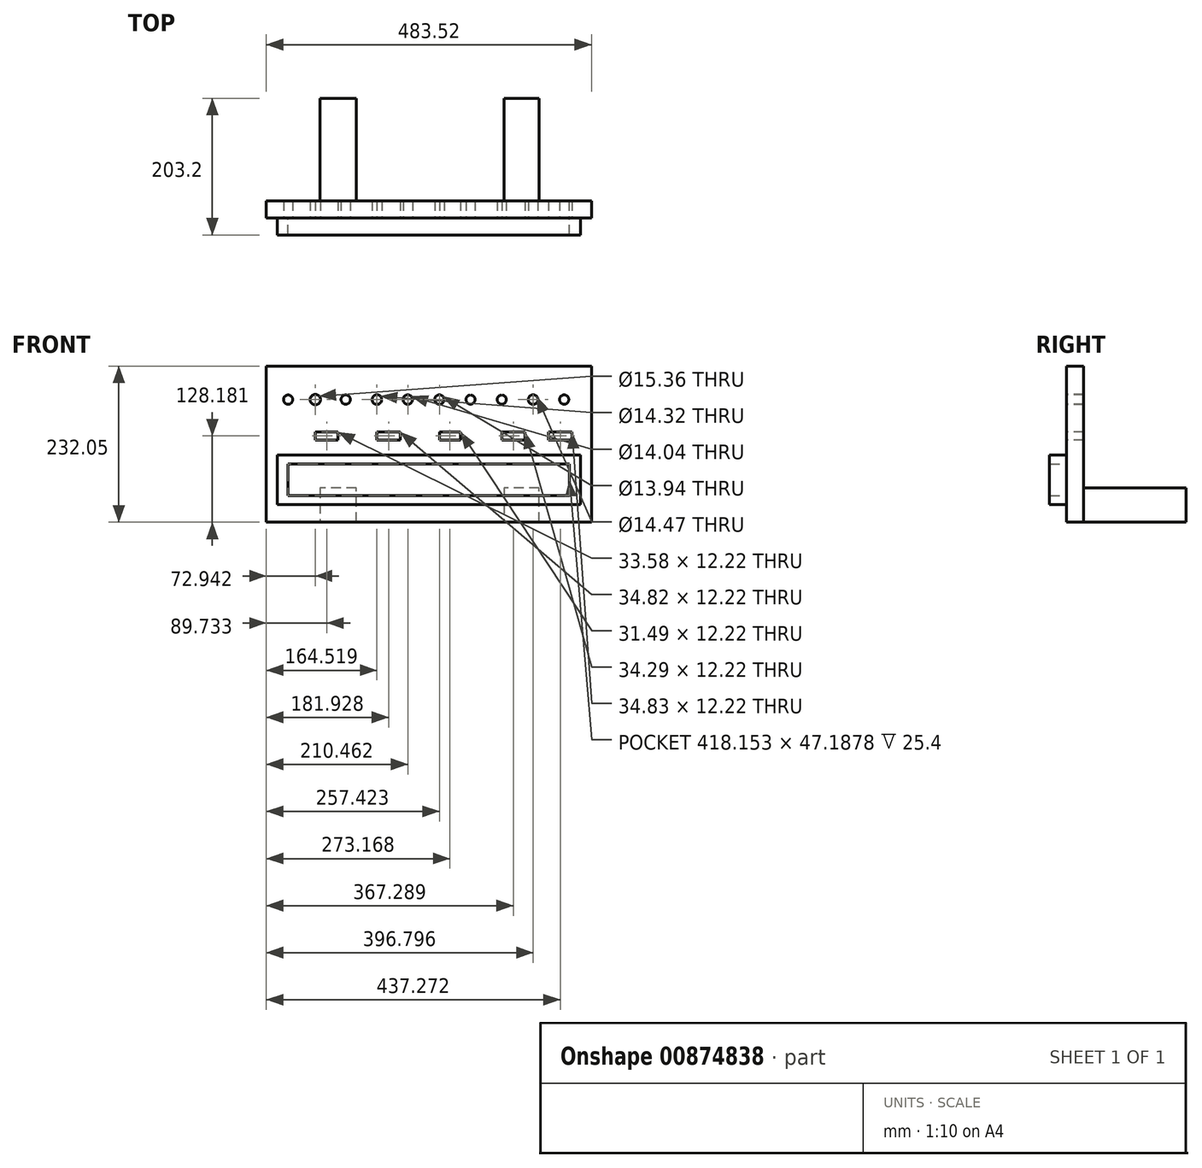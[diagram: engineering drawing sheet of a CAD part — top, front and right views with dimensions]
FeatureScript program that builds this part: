
annotation { "Feature Type Name" : "Feature", "Feature Type Description" : "" }
export const myFeature = defineFeature(function(context is Context, id is Id, definition is map)
    precondition{}
    {
        {
            var Q0;
            Q0=qCreatedBy(makeId("Front.planeOp"),FACE);
            var sketch = newSketch(context, id + "F0", { "sketchPlane" : qUnion([Q0])});
            skLineSegment(sketch, "E0.bottom", {"start": v(0, 0) * mm, "end": v(483.52, 0) * mm});
            skLineSegment(sketch, "E0.top", {"start": v(0, 232.05) * mm, "end": v(483.52, 232.05) * mm});
            skLineSegment(sketch, "E0.left", {"start": v(0, 0) * mm, "end": v(0, 232.05) * mm});
            skLineSegment(sketch, "E0.right", {"start": v(483.52, 0) * mm, "end": v(483.52, 232.05) * mm});
            skSolve(sketch);
        }
        {
            var Q0;
            Q0 = qSketchRegion(id + "F0", true);
            extrude(context, id + "F1", {"entities" : qUnion([Q0]), "depth" : 25.4 * mm, "offsetDistance" : 25.4 * mm});
        }
        {
            var Q0;
            Q0=makeQuery(id+"F1.opExtrude","CAP_FACE",FACE,{"disambiguationData":[OSD([sQuery(id+"F0.wireOp",EDGE,"E0.bottom"),sQuery(id+"F0.wireOp",EDGE,"E0.top"),sQuery(id+"F0.wireOp",EDGE,"E0.left"),sQuery(id+"F0.wireOp",EDGE,"E0.right")])],"isStart":true});
            var sketch = newSketch(context, id + "F2", { "sketchPlane" : qUnion([Q0])});
            skLineSegment(sketch, "E1", {"start": v(-405.91, 0) * mm, "end": v(-353.29, 0) * mm});
            skLineSegment(sketch, "E2", {"start": v(-80.2, 0) * mm, "end": v(-134.1, 0) * mm});
            skLineSegment(sketch, "E3", {"start": v(-134.1, 0) * mm, "end": v(-134.1, 50.78) * mm});
            skLineSegment(sketch, "E4", {"start": v(-134.1, 50.78) * mm, "end": v(-80.2, 50.78) * mm});
            skLineSegment(sketch, "E5", {"start": v(-80.2, 50.78) * mm, "end": v(-80.2, 0) * mm});
            skLineSegment(sketch, "E6", {"start": v(-405.91, 0) * mm, "end": v(-405.91, 50.78) * mm});
            skLineSegment(sketch, "E7", {"start": v(-405.91, 50.78) * mm, "end": v(-353.29, 50.78) * mm});
            skLineSegment(sketch, "E8", {"start": v(-353.29, 50.78) * mm, "end": v(-353.29, 0) * mm});
            skSolve(sketch);
        }
        {
            var Q0;
            Q0 = qSketchRegion(id + "F2", true);
            extrude(context, id + "F3", {"entities" : qUnion([Q0]), "operationType" : NewBodyOperationType.ADD, "depth" : 152.4 * mm, "offsetDistance" : 25.4 * mm});
        }
        {
            var Q0;
            Q0=makeQuery(id+"F1.opExtrude","CAP_FACE",FACE,{"disambiguationData":[OSD([sQuery(id+"F0.wireOp",EDGE,"E0.bottom"),sQuery(id+"F0.wireOp",EDGE,"E0.top"),sQuery(id+"F0.wireOp",EDGE,"E0.left"),sQuery(id+"F0.wireOp",EDGE,"E0.right")])],"isStart":false});
            var sketch = newSketch(context, id + "F4", { "sketchPlane" : qUnion([Q0])});
            skLineSegment(sketch, "E9", {"start": v(32.54, 86.64) * mm, "end": v(32.54, 39.45) * mm});
            skCircle(sketch, "E10", {"center": v(442.92, 182.27) * mm, "radius": 6.94 * mm});
            skCircle(sketch, "E11", {"center": v(396.8, 182.27) * mm, "radius": 7.23 * mm});
            skCircle(sketch, "E12", {"center": v(350.14, 182.27) * mm, "radius": 6.83 * mm});
            skCircle(sketch, "E13", {"center": v(303.67, 182.27) * mm, "radius": 6.83 * mm});
            skCircle(sketch, "E14", {"center": v(257.42, 182.27) * mm, "radius": 6.97 * mm});
            skCircle(sketch, "E15", {"center": v(210.46, 182.27) * mm, "radius": 7.02 * mm});
            skCircle(sketch, "E16", {"center": v(164.52, 182.27) * mm, "radius": 7.16 * mm});
            skCircle(sketch, "E17", {"center": v(118.08, 182.27) * mm, "radius": 6.92 * mm});
            skCircle(sketch, "E18", {"center": v(72.94, 182.27) * mm, "radius": 7.68 * mm});
            skCircle(sketch, "E19", {"center": v(32.54, 182.27) * mm, "radius": 6.87 * mm});
            skLineSegment(sketch, "E20", {"start": v(72.94, 134.29) * mm, "end": v(106.52, 134.29) * mm});
            skLineSegment(sketch, "E21", {"start": v(32.54, 86.64) * mm, "end": v(467.1, 86.64) * mm});
            skLineSegment(sketch, "E22", {"start": v(32.54, 39.45) * mm, "end": v(450.7, 39.45) * mm});
            skLineSegment(sketch, "E23", {"start": v(106.52, 134.29) * mm, "end": v(106.52, 122.07) * mm});
            skLineSegment(sketch, "E24", {"start": v(106.52, 122.07) * mm, "end": v(72.94, 122.07) * mm});
            skLineSegment(sketch, "E25", {"start": v(72.94, 122.07) * mm, "end": v(72.94, 134.29) * mm});
            skLineSegment(sketch, "E26", {"start": v(164.52, 134.29) * mm, "end": v(199.34, 134.29) * mm});
            skLineSegment(sketch, "E27", {"start": v(199.34, 134.29) * mm, "end": v(199.34, 122.07) * mm});
            skLineSegment(sketch, "E28", {"start": v(199.34, 122.07) * mm, "end": v(164.52, 122.07) * mm});
            skLineSegment(sketch, "E29", {"start": v(164.52, 122.07) * mm, "end": v(164.52, 134.29) * mm});
            skLineSegment(sketch, "E30", {"start": v(257.42, 134.29) * mm, "end": v(288.91, 134.29) * mm});
            skLineSegment(sketch, "E31", {"start": v(288.91, 134.29) * mm, "end": v(288.91, 122.07) * mm});
            skLineSegment(sketch, "E32", {"start": v(288.91, 122.07) * mm, "end": v(257.42, 122.07) * mm});
            skLineSegment(sketch, "E33", {"start": v(257.42, 122.07) * mm, "end": v(257.42, 134.29) * mm});
            skLineSegment(sketch, "E34", {"start": v(350.14, 134.29) * mm, "end": v(384.43, 134.29) * mm});
            skLineSegment(sketch, "E35", {"start": v(384.43, 134.29) * mm, "end": v(384.43, 122.07) * mm});
            skLineSegment(sketch, "E36", {"start": v(384.43, 122.07) * mm, "end": v(350.14, 122.07) * mm});
            skLineSegment(sketch, "E37", {"start": v(350.14, 122.07) * mm, "end": v(350.14, 134.29) * mm});
            skLineSegment(sketch, "E38", {"start": v(419.86, 134.29) * mm, "end": v(454.69, 134.29) * mm});
            skPoint(sketch, "E38.startSnap0", {"position": v(419.86, 182.27) * mm});
            skLineSegment(sketch, "E39", {"start": v(419.86, 122.07) * mm, "end": v(419.86, 134.29) * mm});
            skLineSegment(sketch, "E40", {"start": v(454.69, 134.29) * mm, "end": v(454.69, 122.07) * mm});
            skLineSegment(sketch, "E41", {"start": v(454.69, 122.07) * mm, "end": v(419.86, 122.07) * mm});
            skLineSegment(sketch, "E42", {"start": v(32.54, 86.64) * mm, "end": v(16.27, 86.64) * mm});
            skLineSegment(sketch, "E43", {"start": v(467.1, 86.64) * mm, "end": v(450.7, 86.64) * mm});
            skLineSegment(sketch, "E44", {"start": v(450.7, 86.64) * mm, "end": v(450.7, 39.45) * mm});
            skLineSegment(sketch, "E45", {"start": v(16.27, 86.64) * mm, "end": v(16.27, 26.11) * mm});
            skLineSegment(sketch, "E46", {"start": v(16.27, 26.11) * mm, "end": v(467.1, 26.11) * mm});
            skPoint(sketch, "E46.endSnap0", {"position": v(467.1, 86.64) * mm});
            skLineSegment(sketch, "E47", {"start": v(467.1, 26.11) * mm, "end": v(467.1, 86.64) * mm});
            skPoint(sketch, "E48.end.orphan", {"position": v(32.54, 26.11) * mm});
            skPoint(sketch, "E49.orphan", {"position": v(0, 86.64) * mm});
            skPoint(sketch, "E50.orphan", {"position": v(483.52, 86.64) * mm});
            skLineSegment(sketch, "E51", {"start": v(467.1, 86.64) * mm, "end": v(467.1, 99.62) * mm});
            skLineSegment(sketch, "E52", {"start": v(467.1, 99.62) * mm, "end": v(16.27, 99.62) * mm});
            skLineSegment(sketch, "E53", {"start": v(16.27, 99.62) * mm, "end": v(16.27, 86.64) * mm});
            skSolve(sketch);
        }
        {
            var Q0;
            Q0=makeQuery(id+"F4.imprint","IMPRINT",FACE,{"disambiguationData":[TD([[makeQuery(id+"F4.imprint","IMPRINT",EDGE,{"derivedFrom":sQuery(id+"F4.wireOp",EDGE,"E10")}),1.0]])]});
            var Q1;
            Q1=makeQuery(id+"F4.imprint","IMPRINT",FACE,{"disambiguationData":[TD([[makeQuery(id+"F4.imprint","IMPRINT",EDGE,{"derivedFrom":sQuery(id+"F4.wireOp",EDGE,"E11")}),1.0]])]});
            var Q2;
            Q2=makeQuery(id+"F4.imprint","IMPRINT",FACE,{"disambiguationData":[TD([[makeQuery(id+"F4.imprint","IMPRINT",EDGE,{"derivedFrom":sQuery(id+"F4.wireOp",EDGE,"E12")}),1.0]])]});
            var Q3;
            Q3=makeQuery(id+"F4.imprint","IMPRINT",FACE,{"disambiguationData":[TD([[makeQuery(id+"F4.imprint","IMPRINT",EDGE,{"derivedFrom":sQuery(id+"F4.wireOp",EDGE,"E13")}),1.0]])]});
            var Q4;
            Q4=makeQuery(id+"F4.imprint","IMPRINT",FACE,{"disambiguationData":[TD([[makeQuery(id+"F4.imprint","IMPRINT",EDGE,{"derivedFrom":sQuery(id+"F4.wireOp",EDGE,"E14")}),1.0]])]});
            var Q5;
            Q5=makeQuery(id+"F4.imprint","IMPRINT",FACE,{"disambiguationData":[TD([[makeQuery(id+"F4.imprint","IMPRINT",EDGE,{"derivedFrom":sQuery(id+"F4.wireOp",EDGE,"E15")}),1.0]])]});
            var Q6;
            Q6=makeQuery(id+"F4.imprint","IMPRINT",FACE,{"disambiguationData":[TD([[makeQuery(id+"F4.imprint","IMPRINT",EDGE,{"derivedFrom":sQuery(id+"F4.wireOp",EDGE,"E16")}),1.0]])]});
            var Q7;
            Q7=makeQuery(id+"F4.imprint","IMPRINT",FACE,{"disambiguationData":[TD([[makeQuery(id+"F4.imprint","IMPRINT",EDGE,{"derivedFrom":sQuery(id+"F4.wireOp",EDGE,"E17")}),1.0]])]});
            var Q8;
            Q8=makeQuery(id+"F4.imprint","IMPRINT",FACE,{"disambiguationData":[TD([[makeQuery(id+"F4.imprint","IMPRINT",EDGE,{"derivedFrom":sQuery(id+"F4.wireOp",EDGE,"E18")}),1.0]])]});
            var Q9;
            Q9=makeQuery(id+"F4.imprint","IMPRINT",FACE,{"disambiguationData":[TD([[makeQuery(id+"F4.imprint","IMPRINT",EDGE,{"derivedFrom":sQuery(id+"F4.wireOp",EDGE,"E19")}),1.0]])]});
            var Q10;
            Q10=makeQuery(id+"F4.imprint","IMPRINT",FACE,{"disambiguationData":[TD([[makeQuery(id+"F4.imprint","IMPRINT",EDGE,{"derivedFrom":sQuery(id+"F4.wireOp",EDGE,"E20")}),-1.0]])]});
            var Q11;
            Q11=makeQuery(id+"F4.imprint","IMPRINT",FACE,{"disambiguationData":[TD([[makeQuery(id+"F4.imprint","IMPRINT",EDGE,{"derivedFrom":sQuery(id+"F4.wireOp",EDGE,"E27")}),-1.0]])]});
            var Q12;
            Q12=makeQuery(id+"F4.imprint","IMPRINT",FACE,{"disambiguationData":[TD([[makeQuery(id+"F4.imprint","IMPRINT",EDGE,{"derivedFrom":sQuery(id+"F4.wireOp",EDGE,"E31")}),-1.0]])]});
            var Q13;
            Q13=makeQuery(id+"F4.imprint","IMPRINT",FACE,{"disambiguationData":[TD([[makeQuery(id+"F4.imprint","IMPRINT",EDGE,{"derivedFrom":sQuery(id+"F4.wireOp",EDGE,"E35")}),-1.0]])]});
            var Q14;
            Q14=makeQuery(id+"F4.imprint","IMPRINT",FACE,{"disambiguationData":[TD([[makeQuery(id+"F4.imprint","IMPRINT",EDGE,{"derivedFrom":sQuery(id+"F4.wireOp",EDGE,"E39")}),-1.0]])]});
            extrude(context, id + "F5", {"entities" : qUnion([Q0, Q1, Q2, Q3, Q4, Q5, Q6, Q7, Q8, Q9, Q10, Q11, Q12, Q13, Q14]), "operationType" : NewBodyOperationType.REMOVE, "oppositeDirection" : true, "depth" : 25.4 * mm, "offsetDistance" : 25.4 * mm});
        }
        {
            var Q0;
            Q0=makeQuery(id+"F4.imprint","IMPRINT",FACE,{"disambiguationData":[TD([[makeQuery(id+"F4.imprint","IMPRINT",EDGE,{"derivedFrom":sQuery(id+"F4.wireOp",EDGE,"E9")}),-1.0]])]});
            var Q1;
            Q1=makeQuery(id+"F4.imprint","IMPRINT",FACE,{"disambiguationData":[TD([[makeQuery(id+"F4.imprint","IMPRINT",EDGE,{"derivedFrom":sQuery(id+"F4.wireOp",EDGE,"E21")}),1.0]])]});
            extrude(context, id + "F6", {"entities" : qUnion([Q0, Q1]), "operationType" : NewBodyOperationType.ADD, "depth" : 25.4 * mm, "offsetDistance" : 25.4 * mm});
        }
    });
